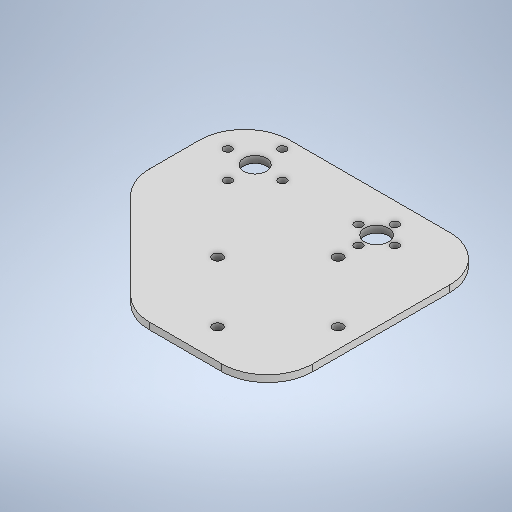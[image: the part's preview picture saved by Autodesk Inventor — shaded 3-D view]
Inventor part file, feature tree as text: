
AUTODESK INVENTOR PART (.ipt)
format: ipt  version: 2025.2 (Build 292293000, 293)  size: 287,744 bytes
history: native  units: mm
features: sketch x6, extrude x3, fillet x1
ambient origin geometry x8: Origin, YZ Plane, XZ Plane, XY Plane, X Axis, Y Axis, Z Axis, Center Point
bodies: Solid1 (feature_tree)
feature tree (10):
  extrude  "Extrusion1"  Depth=50.0mm
  extrude  "Extrusion6"  Depth=3.0mm
  fillet  "Fillet1"  Radius=10.5mm
  extrude  "Extrusion7"  Depth=10.0mm
  sketch  "Sketch1"  dims[d0=150.0mm d1=50.0mm]
  sketch  "Sketch6"  dims[d45=40.0mm d47=360.0deg]
  sketch  "Sketch Circular Pattern1"  dims[d2=3.0mm d3=0.0mm d40=17.0mm d41=10.5mm]
  sketch  "Sketch Circular Pattern2"  dims[d42=53.4mm d43=10.0mm]
  sketch  "Sketch7"  dims[d49=24.0mm d50=3.5mm d51=40.0mm d53=360.0deg d55=0.0mm d56=0.0mm d57=40.0mm d58=50.0mm d59=50.0mm d60=60.0mm d61=20.0mm d62=35.0mm d63=39.6mm d64=90.0deg d65=53.0mm d66=4.3mm d67=40.0mm d69=360.0deg d71=0.0mm d72=0.0mm d26=0.5mm d27=0.872665mm d28=0.5mm d29=0.872665mm]
  sketch  "Sketch Circular Pattern3"  dims[d44=3.5mm]
